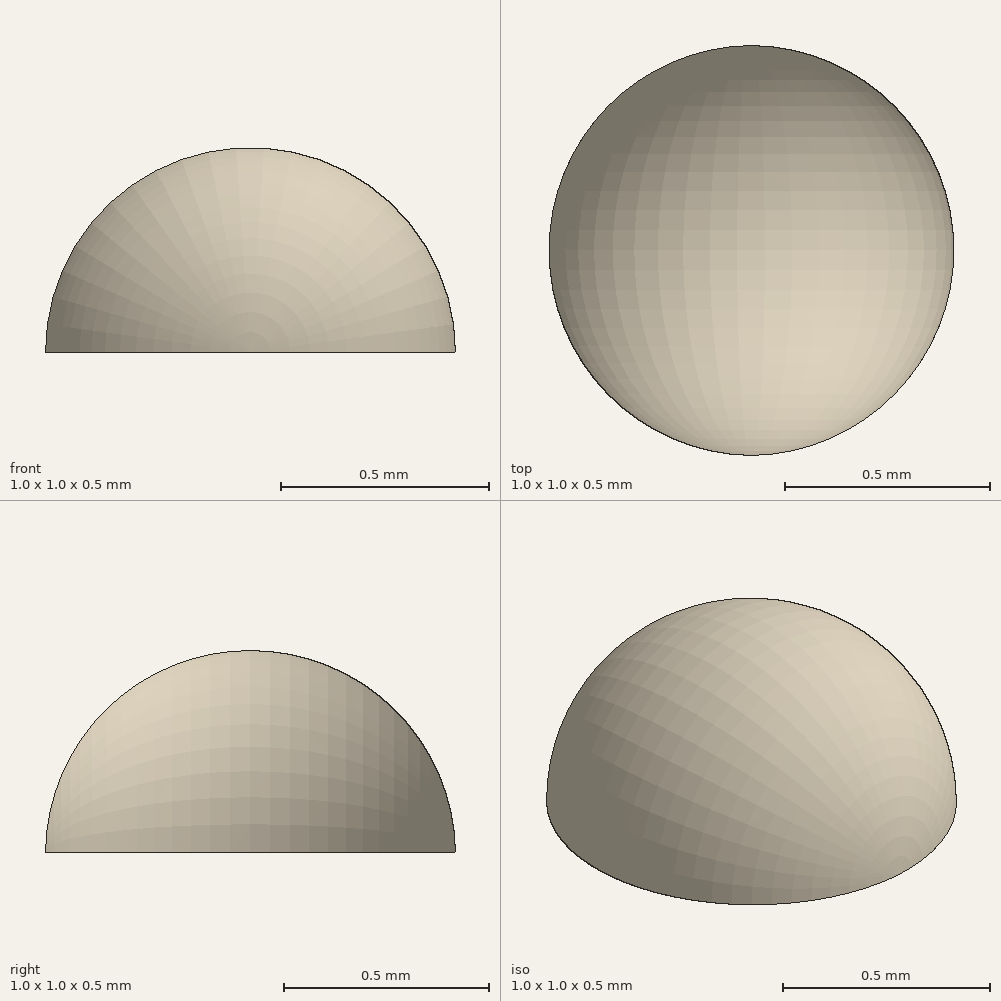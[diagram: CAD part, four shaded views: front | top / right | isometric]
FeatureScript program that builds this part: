
annotation { "Feature Type Name" : "Feature", "Feature Type Description" : "" }
export const myFeature = defineFeature(function(context is Context, id is Id, definition is map)
    precondition{}
    {
        {
            var Q0;
            Q0=qCreatedBy(makeId("Top.planeOp"),FACE);
            var sketch = newSketch(context, id + "F0", { "sketchPlane" : qUnion([Q0])});
            skLineSegment(sketch, "E0", {"start": v(0, -0.5) * mm, "end": v(0, 0.5) * mm});
            skArc(sketch, "E1", {"start": v(0, 0.5) * mm, "mid": v(-0.5, 0) * mm, "end": v(0, -0.5) * mm});
            skSolve(sketch);
        }
        {
            var Q0;
            Q0 = qSketchRegion(id + "F0", true);
            var Q1;
            Q1=sQuery(id+"F0.wireOp",EDGE,"E0");
            revolve(context, id + "F1", {"entities" : qUnion([Q0]), "axis" : qUnion([Q1]), "revolveType" : RevolveType.ONE_DIRECTION, "angle" : 180 * degree});
        }
    });
